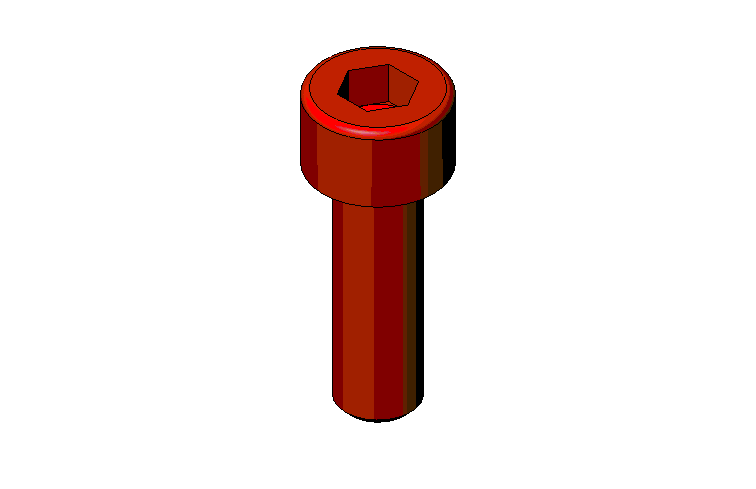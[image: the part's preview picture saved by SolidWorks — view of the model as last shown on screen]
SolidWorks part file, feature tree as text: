
SOLIDWORKS PART (.sldprt)
format: sldprt  version: not decoded by parser v0  size: 211,456 bytes
history: native  units: mm
features: plane x3, sketch x3, material x1, extrude x1, chamfer x1, revolve x1, cut_extrude x1 (+10 scaffold rows collapsed)
feature tree (21):
  scaffold x10  (default folders/planes/origin — collapsed)
  material  "Matériau <non spécifié>"
  plane  "Plan1"
  plane  "Plan2"
  plane  "Plan3"
  sketch  "Esquisse2"  dims[Diamètre nominal=5.0mm]
  extrude  "Base-Extrusion"  Depth=16mm Longueur sous tête=16mm
  chamfer  "Chanfrein1"  Distance=0.5mm Angle=45deg
  sketch  "Esquisse5"  dims[c1.D2=0.5mm c1.Hauteur tête=2.0mm c1.Cote sur plats=5.5mm c1.D3=~2.780036mm c2.D3=30.0deg c2.D4=2.75mm c2.Diamètre tête=8.5mm c2.Diamètre nominal=3.0mm c2.D1=4.25mm c3.D3=3.0mm c4.D3=60.0deg c4.Diamètre nominal=5.0mm c4.Cote sur plats=4.0mm c4.D4=2.5mm c4.D5=2.0mm]
  revolve  "Boss.-Révol.1"  Angle=360deg
  sketch  "Esquisse7"  dims[c1.D1=~2.410714mm c2.D1=30.0deg c2.D2=~1.370242mm c3.D2=30.0deg c3.D3=2.5mm]
  cut_extrude  "Enlèv. mat.-Extru.1"  Depth=2.5mm
decode coverage: 7 of 7 modeling features carry decoded parameters
note: ~ marks probable driven/reference dimensions
note: suppression state not decoded; provenance and decode notes live in map.json
